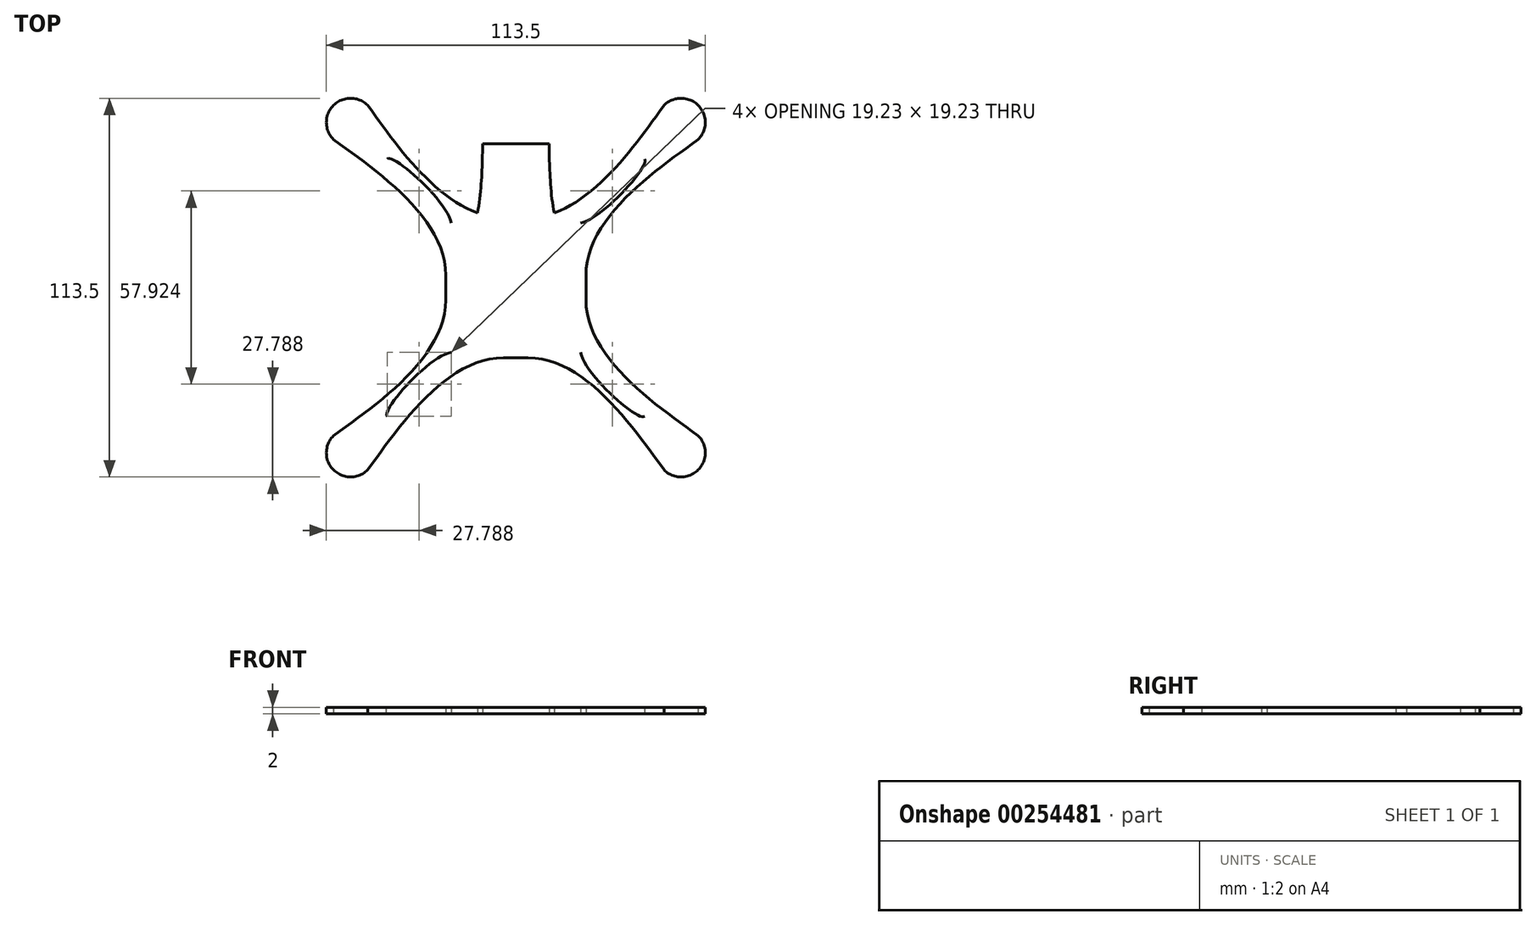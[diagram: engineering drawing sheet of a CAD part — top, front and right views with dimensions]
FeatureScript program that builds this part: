
annotation { "Feature Type Name" : "Feature", "Feature Type Description" : "" }
export const myFeature = defineFeature(function(context is Context, id is Id, definition is map)
    precondition{}
    {
        {
            var Q0;
            Q0=qCreatedBy(makeId("Top.planeOp"),FACE);
            var sketch = newSketch(context, id + "F0", { "sketchPlane" : qUnion([Q0])});
            skLineSegment(sketch, "E0.bottom", {"start": v(49.5, 49.5) * mm, "end": v(-49.5, 49.5) * mm, "construction": true});
            skLineSegment(sketch, "E0.top", {"start": v(49.5, -49.5) * mm, "end": v(-49.5, -49.5) * mm, "construction": true});
            skLineSegment(sketch, "E0.left", {"start": v(49.5, 49.5) * mm, "end": v(49.5, -49.5) * mm, "construction": true});
            skLineSegment(sketch, "E0.right", {"start": v(-49.5, 49.5) * mm, "end": v(-49.5, -49.5) * mm, "construction": true});
            skCircle(sketch, "E1", {"center": v(-49.5, 49.5) * mm, "radius": 38.1 * mm, "construction": true});
            skCircle(sketch, "E2", {"center": v(49.5, 49.5) * mm, "radius": 38.1 * mm, "construction": true});
            skCircle(sketch, "E3", {"center": v(49.5, -49.5) * mm, "radius": 38.1 * mm, "construction": true});
            skCircle(sketch, "E4", {"center": v(-49.5, -49.5) * mm, "radius": 38.1 * mm, "construction": true});
            skCircle(sketch, "E5", {"center": v(-49.5, 49.5) * mm, "radius": 7.25 * mm});
            skPoint(sketch, "E6", {"position": v(-49.5, 0) * mm});
            skPoint(sketch, "E7.center", {"position": v(0, 0) * mm});
            skLineSegment(sketch, "E8", {"start": v(-49.5, 49.5) * mm, "end": v(49.5, -49.5) * mm, "construction": true});
            skLineSegment(sketch, "E9", {"start": v(49.5, 49.5) * mm, "end": v(-49.5, -49.5) * mm, "construction": true});
            skCircle(sketch, "E10.cCircle", {"center": v(0, 0) * mm, "radius": 21 * mm, "construction": true});
            skLineSegment(sketch, "E10.0", {"start": v(-21, 8.7) * mm, "end": v(-8.7, 21) * mm});
            skLineSegment(sketch, "E10.1", {"start": v(-8.7, 21) * mm, "end": v(8.7, 21) * mm});
            skLineSegment(sketch, "E10.2", {"start": v(8.7, 21) * mm, "end": v(21, 8.7) * mm});
            skLineSegment(sketch, "E10.3", {"start": v(21, 8.7) * mm, "end": v(21, -8.7) * mm});
            skLineSegment(sketch, "E10.4", {"start": v(21, -8.7) * mm, "end": v(8.7, -21) * mm});
            skLineSegment(sketch, "E10.5", {"start": v(8.7, -21) * mm, "end": v(-8.7, -21) * mm});
            skLineSegment(sketch, "E10.6", {"start": v(-8.7, -21) * mm, "end": v(-21, -8.7) * mm});
            skLineSegment(sketch, "E10.7", {"start": v(-21, -8.7) * mm, "end": v(-21, 8.7) * mm});
            skPoint(sketch, "E10.0.midPoint", {"position": v(-14.85, 14.85) * mm});
            skLineSegment(sketch, "E11.bottom", {"start": v(15, 15) * mm, "end": v(-15, 15) * mm, "construction": true});
            skLineSegment(sketch, "E11.top", {"start": v(15, -15) * mm, "end": v(-15, -15) * mm, "construction": true});
            skLineSegment(sketch, "E11.left", {"start": v(15, 15) * mm, "end": v(15, -15) * mm, "construction": true});
            skLineSegment(sketch, "E11.right", {"start": v(-15, 15) * mm, "end": v(-15, -15) * mm, "construction": true});
            skLineSegment(sketch, "E12", {"start": v(-44.37, 54.62) * mm, "end": v(-54.62, 44.37) * mm});
            skFitSpline(sketch, "E13", {"points": [v(-54.62, 44.37) * mm, v(-21, 3.7) * mm], "startDerivative": vector(39.22, -28.2) * mm, "endDerivative": vector(0, -51.2) * mm});
            skFitSpline(sketch, "E14", {"points": [v(-19.35, 19.35) * mm, v(-38.58, 38.58) * mm], "startDerivative": vector(-20.3, 3.77) * mm, "endDerivative": vector(5.47, 5.47) * mm});
            skFitSpline(sketch, "E15.MirrorCS", {"points": [v(-44.37, 54.62) * mm, v(-3.7, 21) * mm], "startDerivative": vector(28.2, -39.22) * mm, "endDerivative": vector(51.2, 0) * mm});
            skFitSpline(sketch, "E16.MirrorCS", {"points": [v(-19.35, 19.35) * mm, v(-38.58, 38.58) * mm], "startDerivative": vector(-3.77, 20.3) * mm, "endDerivative": vector(-5.47, -5.47) * mm});
            skLineSegment(sketch, "E17", {"start": v(-9.98, 43.06) * mm, "end": v(9.98, 43.06) * mm});
            skPoint(sketch, "E18", {"position": v(0, 43.06) * mm});
            skPoint(sketch, "E19", {"position": v(0, 21) * mm});
            skFitSpline(sketch, "E20", {"points": [v(-9.98, 43.06) * mm, v(-13.15, 16.55) * mm], "startDerivative": vector(0, -10.01) * mm, "endDerivative": vector(-9.51, -21.95) * mm});
            skLineSegment(sketch, "E21", {"start": v(0, 43.06) * mm, "end": v(0, 0) * mm, "construction": true});
            skFitSpline(sketch, "E22.MirrorCS", {"points": [v(9.98, 43.06) * mm, v(13.15, 16.55) * mm], "startDerivative": vector(0, -10.01) * mm, "endDerivative": vector(9.51, -21.95) * mm});
            skFitSpline(sketch, "E23.MirrorCS", {"points": [v(54.62, 44.37) * mm, v(21, 3.7) * mm], "startDerivative": vector(-39.22, -28.2) * mm, "endDerivative": vector(0, -51.2) * mm});
            skFitSpline(sketch, "E24.MirrorCS", {"points": [v(19.35, 19.35) * mm, v(38.58, 38.58) * mm], "startDerivative": vector(3.77, 20.3) * mm, "endDerivative": vector(5.47, -5.47) * mm});
            skFitSpline(sketch, "E25.MirrorCS", {"points": [v(19.35, 19.35) * mm, v(38.58, 38.58) * mm], "startDerivative": vector(20.3, 3.77) * mm, "endDerivative": vector(-5.47, 5.47) * mm});
            skCircle(sketch, "E26.MirrorC", {"center": v(49.5, 49.5) * mm, "radius": 7.25 * mm});
            skFitSpline(sketch, "E27.MirrorCS", {"points": [v(44.37, 54.62) * mm, v(3.7, 21) * mm], "startDerivative": vector(-28.2, -39.22) * mm, "endDerivative": vector(-51.2, 0) * mm});
            skLineSegment(sketch, "E28", {"start": v(-49.5, 0) * mm, "end": v(49.5, 0) * mm, "construction": true});
            skCircle(sketch, "E29.MirrorC", {"center": v(49.5, -49.5) * mm, "radius": 7.25 * mm});
            skFitSpline(sketch, "E30.MirrorCS", {"points": [v(54.62, -44.37) * mm, v(21, -3.7) * mm], "startDerivative": vector(-39.22, 28.2) * mm, "endDerivative": vector(0, 51.2) * mm});
            skFitSpline(sketch, "E31.MirrorCS", {"points": [v(19.35, -19.35) * mm, v(38.58, -38.58) * mm], "startDerivative": vector(20.3, -3.77) * mm, "endDerivative": vector(-5.47, -5.47) * mm});
            skFitSpline(sketch, "E32.MirrorCS", {"points": [v(19.35, -19.35) * mm, v(38.58, -38.58) * mm], "startDerivative": vector(3.77, -20.3) * mm, "endDerivative": vector(5.47, 5.47) * mm});
            skFitSpline(sketch, "E33.MirrorCS", {"points": [v(44.37, -54.62) * mm, v(3.7, -21) * mm], "startDerivative": vector(-28.2, 39.22) * mm, "endDerivative": vector(-51.2, 0) * mm});
            skFitSpline(sketch, "E34.MirrorCS", {"points": [v(-54.62, -44.37) * mm, v(-21, -3.7) * mm], "startDerivative": vector(39.22, 28.2) * mm, "endDerivative": vector(0, 51.2) * mm});
            skFitSpline(sketch, "E35.MirrorCS", {"points": [v(-19.35, -19.35) * mm, v(-38.58, -38.58) * mm], "startDerivative": vector(-20.3, -3.77) * mm, "endDerivative": vector(5.47, -5.47) * mm});
            skFitSpline(sketch, "E36.MirrorCS", {"points": [v(-19.35, -19.35) * mm, v(-38.58, -38.58) * mm], "startDerivative": vector(-3.77, -20.3) * mm, "endDerivative": vector(-5.47, 5.47) * mm});
            skFitSpline(sketch, "E37.MirrorCS", {"points": [v(-44.37, -54.62) * mm, v(-3.7, -21) * mm], "startDerivative": vector(28.2, 39.22) * mm, "endDerivative": vector(51.2, 0) * mm});
            skCircle(sketch, "E38.MirrorC", {"center": v(-49.5, -49.5) * mm, "radius": 7.25 * mm});
            skSolve(sketch);
        }
        {
            var Q0;
            {var subQ0=sQuery(id+"F0.wireOp",EDGE,"E12");Q0=makeQuery(id+"F0.imprint","IMPRINT",FACE,{"disambiguationData":[TD([[makeQuery(id+"F0.imprint","IMPRINT",EDGE,{"derivedFrom":subQ0}),-1.0]])]});}
            var Q1;
            {var subQ5=sQuery(id+"F0.wireOp",EDGE,"E12");Q1=makeQuery(id+"F0.imprint","IMPRINT",FACE,{"disambiguationData":[TD([[makeQuery(id+"F0.imprint","IMPRINT",EDGE,{"derivedFrom":subQ5}),1.0]])]});}
            var Q2;
            Q2=makeQuery(id+"F0.imprint","IMPRINT",FACE,{"disambiguationData":[TD([[makeQuery(id+"F0.imprint","IMPRINT",EDGE,{"derivedFrom":sQuery(id+"F0.wireOp",EDGE,"E14")}),1.0]])]});
            var Q3;
            {var subQ1=sQuery(id+"F0.wireOp",EDGE,"E17");Q3=makeQuery(id+"F0.imprint","IMPRINT",FACE,{"disambiguationData":[TD([[makeQuery(id+"F0.imprint","IMPRINT",EDGE,{"derivedFrom":subQ1}),-1.0]])]});}
            var Q4;
            {var subQ0=sQuery(id+"F0.wireOp",EDGE,"E10.1");var subQ1=sQuery(id+"F0.wireOp",EDGE,"E10.0");var subQ2=makeQuery(id+"F0.imprint","INTERSECT",VERTEX,{"derivedFrom":[subQ1,subQ0]});Q4=makeQuery(id+"F0.imprint","IMPRINT",FACE,{"disambiguationData":[TD([[makeQuery(id+"F0.imprint","IMPRINT",EDGE,{"disambiguationData":[TD([[subQ2,1.0]])],"derivedFrom":subQ1}),1.0]])]});}
            var Q5;
            {var subQ0=sQuery(id+"F0.wireOp",EDGE,"E10.4");Q5=makeQuery(id+"F0.imprint","IMPRINT",FACE,{"disambiguationData":[TD([[makeQuery(id+"F0.imprint","IMPRINT",EDGE,{"derivedFrom":subQ0}),-1.0]])]});}
            var Q6;
            {var subQ0=sQuery(id+"F0.wireOp",EDGE,"E10.2");var subQ1=sQuery(id+"F0.wireOp",EDGE,"E10.1");var subQ2=makeQuery(id+"F0.imprint","INTERSECT",VERTEX,{"derivedFrom":[subQ1,subQ0]});Q6=makeQuery(id+"F0.imprint","IMPRINT",FACE,{"disambiguationData":[TD([[makeQuery(id+"F0.imprint","IMPRINT",EDGE,{"disambiguationData":[TD([[subQ2,1.0]])],"derivedFrom":subQ1}),1.0]])]});}
            var Q7;
            Q7=makeQuery(id+"F0.imprint","IMPRINT",FACE,{"disambiguationData":[TD([[makeQuery(id+"F0.imprint","IMPRINT",EDGE,{"derivedFrom":sQuery(id+"F0.wireOp",EDGE,"E24.MirrorCS")}),1.0]])]});
            var Q8;
            {var subQ0=sQuery(id+"F0.wireOp",EDGE,"E26.MirrorC");var subQ1=sQuery(id+"F0.wireOp",EDGE,"E23.MirrorCS");var subQ2=makeQuery(id+"F0.imprint","INTERSECT",VERTEX,{"disambiguationData":[OD(0.0)],"derivedFrom":[subQ1,subQ0]});Q8=makeQuery(id+"F0.imprint","IMPRINT",FACE,{"disambiguationData":[TD([[makeQuery(id+"F0.imprint","IMPRINT",EDGE,{"disambiguationData":[TD([[subQ2,-1.0]])],"derivedFrom":subQ1}),-1.0]])]});}
            var Q9;
            {var subQ1=sQuery(id+"F0.wireOp",EDGE,"E10.4");Q9=makeQuery(id+"F0.imprint","IMPRINT",FACE,{"disambiguationData":[TD([[makeQuery(id+"F0.imprint","IMPRINT",EDGE,{"derivedFrom":subQ1}),1.0]])]});}
            var Q10;
            {var subQ1=sQuery(id+"F0.wireOp",EDGE,"E10.6");Q10=makeQuery(id+"F0.imprint","IMPRINT",FACE,{"disambiguationData":[TD([[makeQuery(id+"F0.imprint","IMPRINT",EDGE,{"derivedFrom":subQ1}),1.0]])]});}
            var Q11;
            {var subQ0=sQuery(id+"F0.wireOp",EDGE,"E38.MirrorC");var subQ1=sQuery(id+"F0.wireOp",EDGE,"E34.MirrorCS");var subQ2=makeQuery(id+"F0.imprint","INTERSECT",VERTEX,{"disambiguationData":[OD(0.0)],"derivedFrom":[subQ1,subQ0]});Q11=makeQuery(id+"F0.imprint","IMPRINT",FACE,{"disambiguationData":[TD([[makeQuery(id+"F0.imprint","IMPRINT",EDGE,{"disambiguationData":[TD([[subQ2,-1.0]])],"derivedFrom":subQ1}),-1.0]])]});}
            var Q12;
            {var subQ0=sQuery(id+"F0.wireOp",EDGE,"E30.MirrorCS");var subQ1=sQuery(id+"F0.wireOp",EDGE,"E29.MirrorC");var subQ2=makeQuery(id+"F0.imprint","INTERSECT",VERTEX,{"disambiguationData":[OD(0.0)],"derivedFrom":[subQ1,subQ0]});Q12=makeQuery(id+"F0.imprint","IMPRINT",FACE,{"disambiguationData":[TD([[makeQuery(id+"F0.imprint","IMPRINT",EDGE,{"disambiguationData":[TD([[subQ2,1.0]])],"derivedFrom":subQ1}),1.0]])]});}
            extrude(context, id + "F1", {"entities" : qUnion([Q0, Q1, Q2, Q3, Q4, Q5, Q6, Q7, Q8, Q9, Q10, Q11, Q12]), "depth" : 2 * mm});
        }
    });
